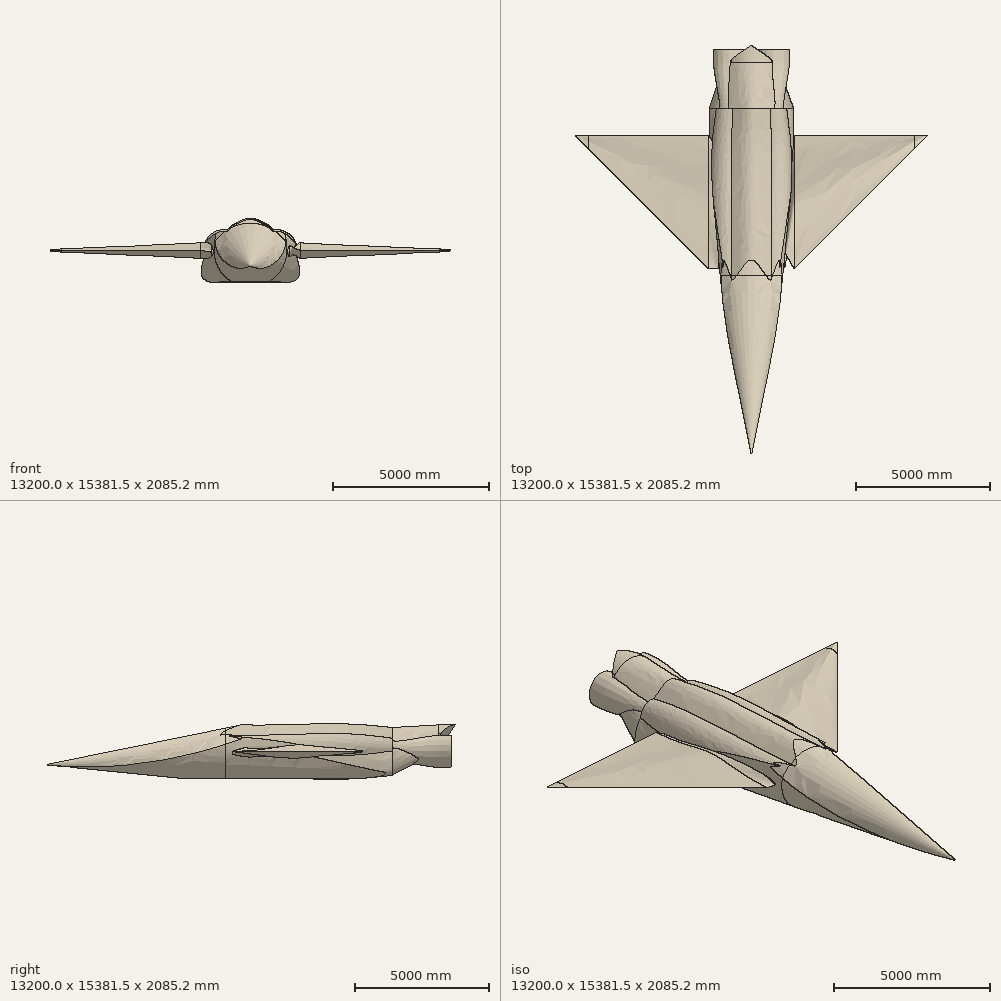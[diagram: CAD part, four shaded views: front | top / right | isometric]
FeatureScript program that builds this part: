
annotation { "Feature Type Name" : "Feature", "Feature Type Description" : "" }
export const myFeature = defineFeature(function(context is Context, id is Id, definition is map)
    precondition{}
    {
        {
            var Q0;
            Q0=qCreatedBy(makeId("Front.planeOp"),FACE);
            cPlane(context, id + "F0", {"entities" : qUnion([Q0]), "cplaneType" : CPlaneType.OFFSET, "offset" : 1750 * mm, "width" : 152.4 * mm, "height" : 152.4 * mm});
        }
        {
            var Q0;
            Q0=qCreatedBy(id+"F0.planeOp",FACE);
            var sketch = newSketch(context, id + "F1", { "sketchPlane" : qUnion([Q0])});
            skLineSegment(sketch, "E0.top", {"start": v(-1394.2, -1000) * mm, "end": v(1394.2, -1000) * mm});
            skPoint(sketch, "E0.middle", {"position": v(0, 0) * mm});
            skFitSpline(sketch, "E1", {"points": [v(-1600, -1000) * mm, v(-848, 530) * mm, v(0, 1000) * mm, v(848, 530) * mm, v(1600, -1000) * mm], "startDerivative": vector(0, 10524.75) * mm, "endDerivative": vector(0, -10524.75) * mm});
            skArc(sketch, "E2", {"start": v(-735.27, 618.52) * mm, "mid": v(-1273.27, 435.52) * mm, "end": v(-1440.68, -107.53) * mm});
            skArc(sketch, "E3.trimOffspring", {"start": v(1440.68, -107.53) * mm, "mid": v(1273.27, 435.52) * mm, "end": v(735.27, 618.52) * mm});
            skFitSpline(sketch, "E4.trimOffspring", {"points": [v(-1600, -1000) * mm, v(-848, 530) * mm, v(0, 1000) * mm, v(848, 530) * mm, v(1600, -1000) * mm], "startDerivative": vector(0, 10524.75) * mm, "endDerivative": vector(0, -10524.75) * mm});
            skFitSpline(sketch, "E5.trimOffspring", {"points": [v(-1600, -1000) * mm, v(-848, 530) * mm, v(0, 1000) * mm, v(848, 530) * mm, v(1600, -1000) * mm], "startDerivative": vector(0, 10524.75) * mm, "endDerivative": vector(0, -10524.75) * mm});
            skArc(sketch, "E6.filletArc", {"start": v(-1593.82, -787.83) * mm, "mid": v(-1539.85, -937.05) * mm, "end": v(-1394.2, -1000) * mm});
            skArc(sketch, "E7.filletArc", {"start": v(1394.2, -1000) * mm, "mid": v(1539.85, -937.05) * mm, "end": v(1593.82, -787.83) * mm});
            skSolve(sketch);
        }
        {
            var Q0;
            Q0=qCreatedBy(makeId("Front.planeOp"),FACE);
            var sketch = newSketch(context, id + "F2", { "sketchPlane" : qUnion([Q0])});
            skLineSegment(sketch, "E8.top", {"start": v(-1394.2, -1000) * mm, "end": v(1394.2, -1000) * mm});
            skPoint(sketch, "E8.middle", {"position": v(0, 0) * mm});
            skFitSpline(sketch, "E9", {"points": [v(-1600, -1000) * mm, v(-848, 530) * mm, v(0, 1000) * mm, v(848, 530) * mm, v(1600, -1000) * mm], "startDerivative": vector(0, 10524.75) * mm, "endDerivative": vector(0, -10524.75) * mm});
            skArc(sketch, "E10", {"start": v(-735.27, 618.52) * mm, "mid": v(-1273.27, 435.52) * mm, "end": v(-1440.68, -107.53) * mm});
            skArc(sketch, "E11.trimOffspring", {"start": v(1440.68, -107.53) * mm, "mid": v(1273.27, 435.52) * mm, "end": v(735.27, 618.52) * mm});
            skFitSpline(sketch, "E12.trimOffspring", {"points": [v(-1600, -1000) * mm, v(-848, 530) * mm, v(0, 1000) * mm, v(848, 530) * mm, v(1600, -1000) * mm], "startDerivative": vector(0, 10524.75) * mm, "endDerivative": vector(0, -10524.75) * mm});
            skFitSpline(sketch, "E13.trimOffspring", {"points": [v(-1600, -1000) * mm, v(-848, 530) * mm, v(0, 1000) * mm, v(848, 530) * mm, v(1600, -1000) * mm], "startDerivative": vector(0, 10524.75) * mm, "endDerivative": vector(0, -10524.75) * mm});
            skArc(sketch, "E14.filletArc", {"start": v(-1593.82, -787.83) * mm, "mid": v(-1539.85, -937.05) * mm, "end": v(-1394.2, -1000) * mm});
            skArc(sketch, "E15.filletArc", {"start": v(1394.2, -1000) * mm, "mid": v(1539.85, -937.05) * mm, "end": v(1593.82, -787.83) * mm});
            skSolve(sketch);
        }
        {
            var Q0;
            Q0=qCreatedBy(makeId("Front.planeOp"),FACE);
            cPlane(context, id + "F3", {"entities" : qUnion([Q0]), "cplaneType" : CPlaneType.OFFSET, "offset" : 3500 * mm, "oppositeDirection" : true, "width" : 150 * mm, "height" : 150 * mm});
        }
        {
            var Q0;
            Q0=qCreatedBy(id+"F3.planeOp",FACE);
            var sketch = newSketch(context, id + "F4", { "sketchPlane" : qUnion([Q0])});
            skLineSegment(sketch, "E16.top", {"start": v(-1394.2, -1000) * mm, "end": v(1394.2, -1000) * mm});
            skPoint(sketch, "E16.middle", {"position": v(0, 0) * mm});
            skFitSpline(sketch, "E17", {"points": [v(-1600, -1000) * mm, v(-848, 530) * mm, v(0, 1000) * mm, v(848, 530) * mm, v(1600, -1000) * mm], "startDerivative": vector(0, 10524.75) * mm, "endDerivative": vector(0, -10524.75) * mm});
            skArc(sketch, "E18", {"start": v(-735.27, 618.52) * mm, "mid": v(-1273.27, 435.52) * mm, "end": v(-1440.68, -107.53) * mm});
            skArc(sketch, "E19.trimOffspring", {"start": v(1440.68, -107.53) * mm, "mid": v(1273.27, 435.52) * mm, "end": v(735.27, 618.52) * mm});
            skFitSpline(sketch, "E20.trimOffspring", {"points": [v(-1600, -1000) * mm, v(-848, 530) * mm, v(0, 1000) * mm, v(848, 530) * mm, v(1600, -1000) * mm], "startDerivative": vector(0, 10524.75) * mm, "endDerivative": vector(0, -10524.75) * mm});
            skFitSpline(sketch, "E21.trimOffspring", {"points": [v(-1600, -1000) * mm, v(-848, 530) * mm, v(0, 1000) * mm, v(848, 530) * mm, v(1600, -1000) * mm], "startDerivative": vector(0, 10524.75) * mm, "endDerivative": vector(0, -10524.75) * mm});
            skArc(sketch, "E22.filletArc", {"start": v(-1593.82, -787.83) * mm, "mid": v(-1539.85, -937.05) * mm, "end": v(-1394.2, -1000) * mm});
            skArc(sketch, "E23.filletArc", {"start": v(1394.2, -1000) * mm, "mid": v(1539.85, -937.05) * mm, "end": v(1593.82, -787.83) * mm});
            skSolve(sketch);
        }
        {
            var Q0;
            Q0=qCreatedBy(makeId("Front.planeOp"),FACE);
            cPlane(context, id + "F5", {"entities" : qUnion([Q0]), "cplaneType" : CPlaneType.OFFSET, "offset" : 4500 * mm, "oppositeDirection" : true, "width" : 150 * mm, "height" : 150 * mm});
        }
        {
            var Q0;
            Q0=qCreatedBy(id+"F5.planeOp",FACE);
            var sketch = newSketch(context, id + "F6", { "sketchPlane" : qUnion([Q0])});
            skLineSegment(sketch, "E24.top", {"start": v(-1413.07, -900) * mm, "end": v(1413.07, -900) * mm});
            skPoint(sketch, "E24.middle", {"position": v(0, 0) * mm});
            skFitSpline(sketch, "E25", {"points": [v(-1600, -900) * mm, v(-784.42, 441.24) * mm, v(0, 900) * mm, v(784.42, 441.24) * mm, v(1600, -900) * mm], "startDerivative": vector(0, 9508.62) * mm, "endDerivative": vector(0, -9508.62) * mm});
            skArc(sketch, "E26", {"start": v(-719.25, 488.69) * mm, "mid": v(-1131.76, 394.84) * mm, "end": v(-1324.66, 18.33) * mm});
            skArc(sketch, "E27.trimOffspring", {"start": v(1324.66, 18.33) * mm, "mid": v(1131.76, 394.84) * mm, "end": v(719.25, 488.69) * mm});
            skFitSpline(sketch, "E28.trimOffspring", {"points": [v(-1600, -900) * mm, v(-784.42, 441.24) * mm, v(0, 900) * mm, v(784.42, 441.24) * mm, v(1600, -900) * mm], "startDerivative": vector(0, 9508.62) * mm, "endDerivative": vector(0, -9508.62) * mm});
            skFitSpline(sketch, "E29.trimOffspring", {"points": [v(-1600, -900) * mm, v(-784.42, 441.24) * mm, v(0, 900) * mm, v(784.42, 441.24) * mm, v(1600, -900) * mm], "startDerivative": vector(0, 9508.62) * mm, "endDerivative": vector(0, -9508.62) * mm});
            skArc(sketch, "E30.filletArc", {"start": v(-1592.48, -705.43) * mm, "mid": v(-1545.4, -842.02) * mm, "end": v(-1413.07, -900) * mm});
            skArc(sketch, "E31.filletArc", {"start": v(1413.07, -900) * mm, "mid": v(1545.4, -842.02) * mm, "end": v(1592.48, -705.43) * mm});
            skLineSegment(sketch, "E32", {"start": v(-719.25, 488.69) * mm, "end": v(-1324.66, 18.33) * mm, "construction": true});
            skLineSegment(sketch, "E33", {"start": v(719.25, 488.69) * mm, "end": v(1324.66, 18.33) * mm, "construction": true});
            skSolve(sketch);
        }
        {
            var Q0;
            Q0=qCreatedBy(makeId("Front.planeOp"),FACE);
            cPlane(context, id + "F7", {"entities" : qUnion([Q0]), "cplaneType" : CPlaneType.OFFSET, "offset" : 6232.05 * mm, "oppositeDirection" : true, "width" : 150 * mm, "height" : 150 * mm});
        }
        {
            var Q0;
            Q0=qCreatedBy(id+"F7.planeOp",FACE);
            var sketch = newSketch(context, id + "F8", { "sketchPlane" : qUnion([Q0])});
            skArc(sketch, "E34", {"start": v(998.61, 52.63) * mm, "mid": v(0, 1000) * mm, "end": v(-998.61, 52.63) * mm});
            skLineSegment(sketch, "E35", {"start": v(0, 0) * mm, "end": v(-948.68, 0) * mm});
            skLineSegment(sketch, "E36", {"start": v(0, 0) * mm, "end": v(948.68, 0) * mm});
            skPoint(sketch, "E37.visualSharp", {"position": v(-1000, 0) * mm});
            skArc(sketch, "E37.filletArc", {"start": v(-998.61, 52.63) * mm, "mid": v(-984.96, 15.59) * mm, "end": v(-948.68, 0) * mm});
            skPoint(sketch, "E38.visualSharp", {"position": v(1000, 0) * mm});
            skArc(sketch, "E38.filletArc", {"start": v(948.68, 0) * mm, "mid": v(984.96, 15.59) * mm, "end": v(998.61, 52.63) * mm});
            skLineSegment(sketch, "E39", {"start": v(0, 1000) * mm, "end": v(0, 675) * mm, "construction": true});
            skPoint(sketch, "E39.endSnap0", {"position": v(0, 1000) * mm});
            skLineSegment(sketch, "E40", {"start": v(0, 675) * mm, "end": v(737.82, 675) * mm, "construction": true});
            skLineSegment(sketch, "E41", {"start": v(0, 675) * mm, "end": v(-737.82, 675) * mm, "construction": true});
            skSolve(sketch);
        }
        {
            var Q0;
            Q0=qSketchRegion(id+"F1",true);
            var Q1;
            Q1=qSketchRegion(id+"F2",true);
            var Q2;
            Q2=qSketchRegion(id+"F4",true);
            var Q3;
            Q3=qSketchRegion(id+"F6",true);
            loft(context, id + "F9", {"sheetProfilesArray" : [{ "sheetProfileEntities" : qUnion([Q0]) }, { "sheetProfileEntities" : qUnion([Q1]) }, { "sheetProfileEntities" : qUnion([Q2]) }, { "sheetProfileEntities" : qUnion([Q3]) }]});
        }
        {
            var Q0;
            Q0=sQuery(id+"F6.wireOp",EDGE,"E32");
            var Q1;
            Q1=sQuery(id+"F8.wireOp",VERTEX,"E41.end");
            cPlane(context, id + "F10", {"entities" : qUnion([Q0, Q1]), "cplaneType" : CPlaneType.LINE_ANGLE, "offset" : 25 * mm, "angle" : 0 * degree, "width" : 150 * mm, "height" : 150 * mm});
        }
        {
            var Q0;
            Q0=qCreatedBy(id+"F10.planeOp",FACE);
            var sketch = newSketch(context, id + "F11", { "sketchPlane" : qUnion([Q0])});
            skLineSegment(sketch, "E42", {"start": v(-589.34, -4526.34) * mm, "end": v(-612.8, -6268.32) * mm});
            skLineSegment(sketch, "E43", {"start": v(-1354.08, -4472.19) * mm, "end": v(-612.8, -6268.32) * mm});
            skSolve(sketch);
        }
        {
            var Q0;
            Q0=sQuery(id+"F6.wireOp",EDGE,"E33");
            var Q1;
            Q1=sQuery(id+"F8.wireOp",VERTEX,"E40.end");
            cPlane(context, id + "F12", {"entities" : qUnion([Q0, Q1]), "cplaneType" : CPlaneType.LINE_ANGLE, "offset" : 25 * mm, "angle" : 0 * degree, "width" : 150 * mm, "height" : 150 * mm});
        }
        {
            var Q0;
            Q0=qCreatedBy(id+"F12.planeOp",FACE);
            var sketch = newSketch(context, id + "F13", { "sketchPlane" : qUnion([Q0])});
            skLineSegment(sketch, "E44", {"start": v(589.34, 4526.34) * mm, "end": v(612.8, 6268.32) * mm});
            skLineSegment(sketch, "E45", {"start": v(1354.08, 4472.19) * mm, "end": v(612.8, 6268.32) * mm});
            skSolve(sketch);
        }
        {
            var Q1;
            Q1=makeQuery(id+"F6.imprint","IMPRINT",FACE,{"disambiguationData":[TD([[makeQuery(id+"F6.imprint","IMPRINT",EDGE,{"derivedFrom":sQuery(id+"F6.wireOp",EDGE,"E24.top")}),1.0]])]});
            var Q2;
            Q2=makeQuery(id+"F8.imprint","IMPRINT",FACE,{"disambiguationData":[TD([[makeQuery(id+"F8.imprint","IMPRINT",EDGE,{"derivedFrom":sQuery(id+"F8.wireOp",EDGE,"E34")}),1.0]])]});
            var Q3;
            Q3=sQuery(id+"F11.wireOp",EDGE,"E42");
            var Q4;
            Q4=sQuery(id+"F13.wireOp",EDGE,"E44");
            loft(context, id + "F14", {"operationType" : NewBodyOperationType.ADD, "addGuides" : true, "sheetProfilesArray" : [{ "sheetProfileEntities" : qUnion([Q1]) }, { "sheetProfileEntities" : qUnion([Q2]) }], "guidesArray" : [{ "guideEntities" : qUnion([Q3]), "guideDerivativeType" : LoftGuideDerivativeType.DEFAULT, "guideDerivativeMagnitude" : 1 }, { "guideEntities" : qUnion([Q4]), "guideDerivativeType" : LoftGuideDerivativeType.DEFAULT, "guideDerivativeMagnitude" : 1 }]});
        }
        {
            var Q0;
            Q0=makeQuery(id+"F14.opLoft","CAP_FACE",FACE,{"disambiguationData":[OSD([makeQuery(id+"F8.imprint","IMPRINT",FACE,{"disambiguationData":[TD([[makeQuery(id+"F8.imprint","IMPRINT",EDGE,{"derivedFrom":sQuery(id+"F8.wireOp",EDGE,"E34")}),1.0]])]})])],"isStart":true});
            extrude(context, id + "F15", {"entities" : qUnion([Q0]), "operationType" : NewBodyOperationType.ADD, "depth" : 649.4 * mm});
        }
        {
            var Q0;
            Q0=qCreatedBy(makeId("Right.planeOp"),FACE);
            var sketch = newSketch(context, id + "F16", { "sketchPlane" : qUnion([Q0])});
            skLineSegment(sketch, "E46", {"start": v(0, 0) * mm, "end": v(4500, 0) * mm});
            skLineSegment(sketch, "E47", {"start": v(4500, 0) * mm, "end": v(6232.05, 0) * mm});
            skLineSegment(sketch, "E48", {"start": v(4500, 0) * mm, "end": v(4500, 1000) * mm});
            skLineSegment(sketch, "E49", {"start": v(4500, 1000) * mm, "end": v(6881.46, 1000) * mm});
            skLineSegment(sketch, "E50", {"start": v(6881.46, 1000) * mm, "end": v(6881.46, -1000) * mm});
            skLineSegment(sketch, "E51", {"start": v(6881.46, 1000) * mm, "end": v(6232.05, 0) * mm});
            skLineSegment(sketch, "E52", {"start": v(6232.05, 0) * mm, "end": v(5582.64, -1000) * mm});
            skLineSegment(sketch, "E53", {"start": v(5582.64, -1000) * mm, "end": v(6881.46, -1000) * mm});
            skSolve(sketch);
        }
        {
            var Q0;
            Q0=makeQuery(id+"F16.imprint","IMPRINT",FACE,{"disambiguationData":[TD([[makeQuery(id+"F16.imprint","IMPRINT",EDGE,{"derivedFrom":sQuery(id+"F16.wireOp",EDGE,"E50")}),-1.0]])]});
            var Q1;
            Q1=sQuery(id+"F16.wireOp",EDGE,"E49");
            revolve(context, id + "F17", {"operationType" : NewBodyOperationType.REMOVE, "entities" : qUnion([Q0]), "axis" : qUnion([Q1]), "revolveType" : RevolveType.SYMMETRIC, "oppositeDirection" : true, "angle" : 182 * degree});
        }
        {
            var Q0;
            Q0=makeQuery(id+"F9.opLoft","CAP_FACE",FACE,{"disambiguationData":[OSD([makeQuery(id+"F1.imprint","IMPRINT",FACE,{"disambiguationData":[TD([[makeQuery(id+"F1.imprint","IMPRINT",EDGE,{"derivedFrom":sQuery(id+"F1.wireOp",EDGE,"E0.top")}),1.0]])]})])],"isStart":true});
            extrude(context, id + "F18", {"entities" : qUnion([Q0]), "depth" : 6750 * mm});
        }
        {
            var Q0;
            Q0=qCreatedBy(makeId("Right.planeOp"),FACE);
            var sketch = newSketch(context, id + "F19", { "sketchPlane" : qUnion([Q0])});
            skLineSegment(sketch, "E54", {"start": v(0, 0) * mm, "end": v(-3500, 0) * mm});
            skLineSegment(sketch, "E55", {"start": v(-3500, 0) * mm, "end": v(-3500, -1000) * mm});
            skLineSegment(sketch, "E56", {"start": v(-3500, -1000) * mm, "end": v(-8500, -1000) * mm});
            skLineSegment(sketch, "E57", {"start": v(-8500, -1000) * mm, "end": v(-8500, -499.31) * mm});
            skLineSegment(sketch, "E58", {"start": v(-1151.4, 0) * mm, "end": v(-1151.4, 1000) * mm});
            skLineSegment(sketch, "E59", {"start": v(-1151.4, 1000) * mm, "end": v(-8500, -499.31) * mm});
            skLineSegment(sketch, "E60", {"start": v(-8500, -499.31) * mm, "end": v(-3500, -1000) * mm});
            skLineSegment(sketch, "E61", {"start": v(-1151.4, 1000) * mm, "end": v(-8500, 1000) * mm});
            skLineSegment(sketch, "E62", {"start": v(-8500, 1000) * mm, "end": v(-8500, -499.31) * mm});
            skLineSegment(sketch, "E63", {"start": v(-8500, -1000) * mm, "end": v(-8500, -1980) * mm});
            skLineSegment(sketch, "E64", {"start": v(-3500, -1000) * mm, "end": v(6286.5, -1980) * mm});
            skLineSegment(sketch, "E65", {"start": v(6286.5, -1980) * mm, "end": v(-8500, -1980) * mm});
            skLineSegment(sketch, "E66", {"start": v(-8500, -499.31) * mm, "end": v(-3500, -499.31) * mm});
            skSolve(sketch);
        }
        {
            var Q0;
            Q0=makeQuery(id+"F19.imprint","IMPRINT",FACE,{"disambiguationData":[TD([[makeQuery(id+"F19.imprint","IMPRINT",EDGE,{"derivedFrom":sQuery(id+"F19.wireOp",EDGE,"E59")}),-1.0]])]});
            var Q1;
            Q1=sQuery(id+"F19.wireOp",EDGE,"E66");
            revolve(context, id + "F20", {"operationType" : NewBodyOperationType.REMOVE, "entities" : qUnion([Q0]), "axis" : qUnion([Q1]), "revolveType" : RevolveType.SYMMETRIC, "oppositeDirection" : true, "angle" : 250 * degree});
        }
        {
            var Q0;
            Q0=makeQuery(id+"F19.imprint","IMPRINT",FACE,{"disambiguationData":[TD([[makeQuery(id+"F19.imprint","IMPRINT",EDGE,{"derivedFrom":sQuery(id+"F19.wireOp",EDGE,"E56")}),-1.0]])]});
            var Q1;
            Q1=makeQuery(id+"F19.imprint","IMPRINT",FACE,{"disambiguationData":[TD([[makeQuery(id+"F19.imprint","IMPRINT",EDGE,{"derivedFrom":sQuery(id+"F19.wireOp",EDGE,"E56")}),1.0]])]});
            var Q2;
            Q2=sQuery(id+"F19.wireOp",EDGE,"E54");
            revolve(context, id + "F21", {"operationType" : NewBodyOperationType.REMOVE, "entities" : qUnion([Q0, Q1]), "axis" : qUnion([Q2]), "revolveType" : RevolveType.SYMMETRIC, "oppositeDirection" : true, "angle" : 240 * degree});
        }
        {
            var Q0;
            Q0=qCreatedBy(makeId("Front.planeOp"),FACE);
            cPlane(context, id + "F22", {"entities" : qUnion([Q0]), "cplaneType" : CPlaneType.OFFSET, "offset" : 3500 * mm, "oppositeDirection" : true, "width" : 150 * mm, "height" : 150 * mm});
        }
        {
            var Q0;
            Q0=qCreatedBy(id+"F22.planeOp",FACE);
            var sketch = newSketch(context, id + "F23", { "sketchPlane" : qUnion([Q0])});
            skCircle(sketch, "E67", {"center": v(-825, 0) * mm, "radius": 600 * mm});
            skCircle(sketch, "E68", {"center": v(825, 0) * mm, "radius": 600 * mm});
            skSolve(sketch);
        }
        {
            var Q0;
            Q0=qCreatedBy(makeId("Front.planeOp"),FACE);
            cPlane(context, id + "F24", {"entities" : qUnion([Q0]), "cplaneType" : CPlaneType.OFFSET, "offset" : 4500 * mm, "oppositeDirection" : true, "width" : 150 * mm, "height" : 150 * mm});
        }
        {
            var Q0;
            Q0=qCreatedBy(id+"F24.planeOp",FACE);
            var sketch = newSketch(context, id + "F25", { "sketchPlane" : qUnion([Q0])});
            skCircle(sketch, "E69", {"center": v(-825, 0) * mm, "radius": 400 * mm});
            skCircle(sketch, "E70", {"center": v(825, 0) * mm, "radius": 400 * mm});
            skSolve(sketch);
        }
        {
            var Q0;
            Q0=qCreatedBy(makeId("Front.planeOp"),FACE);
            cPlane(context, id + "F26", {"entities" : qUnion([Q0]), "cplaneType" : CPlaneType.OFFSET, "offset" : 6232.05 * mm, "oppositeDirection" : true, "width" : 150 * mm, "height" : 150 * mm});
        }
        {
            var Q0;
            Q0=qCreatedBy(id+"F26.planeOp",FACE);
            var sketch = newSketch(context, id + "F27", { "sketchPlane" : qUnion([Q0])});
            skCircle(sketch, "E71", {"center": v(-825, 0) * mm, "radius": 600 * mm});
            skCircle(sketch, "E72", {"center": v(825, 0) * mm, "radius": 600 * mm});
            skSolve(sketch);
        }
        {
            var Q0;
            Q0=qCreatedBy(makeId("Front.planeOp"),FACE);
            cPlane(context, id + "F28", {"entities" : qUnion([Q0]), "cplaneType" : CPlaneType.OFFSET, "offset" : 6732.05 * mm, "oppositeDirection" : true, "width" : 150 * mm, "height" : 150 * mm});
        }
        {
            var Q0;
            Q0=qCreatedBy(id+"F28.planeOp",FACE);
            var sketch = newSketch(context, id + "F29", { "sketchPlane" : qUnion([Q0])});
            skCircle(sketch, "E73", {"center": v(-825, 0) * mm, "radius": 600 * mm});
            skCircle(sketch, "E74", {"center": v(825, 0) * mm, "radius": 600 * mm});
            skSolve(sketch);
        }
        {
            var Q0;
            Q0=makeQuery(id+"F23.imprint","IMPRINT",FACE,{"disambiguationData":[TD([[makeQuery(id+"F23.imprint","IMPRINT",EDGE,{"derivedFrom":sQuery(id+"F23.wireOp",EDGE,"E67")}),1.0]])]});
            var Q1;
            Q1=makeQuery(id+"F25.imprint","IMPRINT",FACE,{"disambiguationData":[TD([[makeQuery(id+"F25.imprint","IMPRINT",EDGE,{"derivedFrom":sQuery(id+"F25.wireOp",EDGE,"E69")}),1.0]])]});
            var Q2;
            Q2=makeQuery(id+"F27.imprint","IMPRINT",FACE,{"disambiguationData":[TD([[makeQuery(id+"F27.imprint","IMPRINT",EDGE,{"derivedFrom":sQuery(id+"F27.wireOp",EDGE,"E71")}),1.0]])]});
            var Q3;
            Q3=makeQuery(id+"F29.imprint","IMPRINT",FACE,{"disambiguationData":[TD([[makeQuery(id+"F29.imprint","IMPRINT",EDGE,{"derivedFrom":sQuery(id+"F29.wireOp",EDGE,"E73")}),1.0]])]});
            loft(context, id + "F30", {"sheetProfilesArray" : [{ "sheetProfileEntities" : qUnion([Q0]) }, { "sheetProfileEntities" : qUnion([Q1]) }, { "sheetProfileEntities" : qUnion([Q2]) }, { "sheetProfileEntities" : qUnion([Q3]) }]});
        }
        {
            var Q0;
            Q0=makeQuery(id+"F23.imprint","IMPRINT",FACE,{"disambiguationData":[TD([[makeQuery(id+"F23.imprint","IMPRINT",EDGE,{"derivedFrom":sQuery(id+"F23.wireOp",EDGE,"E68")}),1.0]])]});
            var Q1;
            Q1=makeQuery(id+"F25.imprint","IMPRINT",FACE,{"disambiguationData":[TD([[makeQuery(id+"F25.imprint","IMPRINT",EDGE,{"derivedFrom":sQuery(id+"F25.wireOp",EDGE,"E70")}),1.0]])]});
            var Q2;
            Q2=makeQuery(id+"F27.imprint","IMPRINT",FACE,{"disambiguationData":[TD([[makeQuery(id+"F27.imprint","IMPRINT",EDGE,{"derivedFrom":sQuery(id+"F27.wireOp",EDGE,"E72")}),1.0]])]});
            var Q3;
            Q3=makeQuery(id+"F29.imprint","IMPRINT",FACE,{"disambiguationData":[TD([[makeQuery(id+"F29.imprint","IMPRINT",EDGE,{"derivedFrom":sQuery(id+"F29.wireOp",EDGE,"E74")}),1.0]])]});
            loft(context, id + "F31", {"sheetProfilesArray" : [{ "sheetProfileEntities" : qUnion([Q0]) }, { "sheetProfileEntities" : qUnion([Q1]) }, { "sheetProfileEntities" : qUnion([Q2]) }, { "sheetProfileEntities" : qUnion([Q3]) }]});
        }
        {
            var Q0;
            Q0=qCreatedBy(makeId("Top.planeOp"),FACE);
            var sketch = newSketch(context, id + "F32", { "sketchPlane" : qUnion([Q0])});
            skLineSegment(sketch, "E75", {"start": v(0, 0) * mm, "end": v(0, 1000) * mm});
            skLineSegment(sketch, "E76", {"start": v(0, 1000) * mm, "end": v(-1600, 1000) * mm});
            skLineSegment(sketch, "E77", {"start": v(-1600, 1000) * mm, "end": v(-1600, -1500) * mm});
            skLineSegment(sketch, "E78", {"start": v(-1600, 1000) * mm, "end": v(-1600, 3500) * mm});
            skLineSegment(sketch, "E79", {"start": v(-1600, 3500) * mm, "end": v(-6100, 3500) * mm});
            skLineSegment(sketch, "E80", {"start": v(-6100, 3500) * mm, "end": v(-6600, 3500) * mm});
            skLineSegment(sketch, "E81", {"start": v(-6100, 3500) * mm, "end": v(-6100, 3000) * mm});
            skLineSegment(sketch, "E82", {"start": v(-1600, -1500) * mm, "end": v(-6100, 3000) * mm});
            skLineSegment(sketch, "E83", {"start": v(0, 1000) * mm, "end": v(1600, 1000) * mm});
            skLineSegment(sketch, "E84", {"start": v(1600, 1000) * mm, "end": v(1600, -1500) * mm});
            skLineSegment(sketch, "E85", {"start": v(1600, 1000) * mm, "end": v(1600, 3500) * mm});
            skLineSegment(sketch, "E86", {"start": v(1600, 3500) * mm, "end": v(6100, 3500) * mm});
            skLineSegment(sketch, "E87", {"start": v(6100, 3500) * mm, "end": v(6600, 3500) * mm});
            skLineSegment(sketch, "E88", {"start": v(6100, 3500) * mm, "end": v(6100, 3000) * mm});
            skLineSegment(sketch, "E89", {"start": v(1600, -1500) * mm, "end": v(6100, 3000) * mm});
            skSolve(sketch);
        }
        {
            var Q0;
            Q0=qCreatedBy(makeId("Right.planeOp"),FACE);
            var sketch = newSketch(context, id + "F33", { "sketchPlane" : qUnion([Q0])});
            skFitSpline(sketch, "E90", {"points": [v(-1500, -50) * mm, v(0, 250) * mm, v(3000, -50) * mm, v(0, -250) * mm, v(-1500, -50) * mm]});
            skSolve(sketch);
        }
        {
            var Q0;
            Q0=qCreatedBy(makeId("Right.planeOp"),FACE);
            cPlane(context, id + "F34", {"entities" : qUnion([Q0]), "cplaneType" : CPlaneType.OFFSET, "offset" : 1600 * mm, "oppositeDirection" : true, "width" : 150 * mm, "height" : 150 * mm});
        }
        {
            var Q0;
            Q0=qCreatedBy(id+"F34.planeOp",FACE);
            var sketch = newSketch(context, id + "F35", { "sketchPlane" : qUnion([Q0])});
            skFitSpline(sketch, "E91", {"points": [v(-1500, 0) * mm, v(1000, 250) * mm, v(3500, 0) * mm], "startDerivative": vector(7500, 0) * mm, "endDerivative": vector(7500, 0) * mm});
            skFitSpline(sketch, "E92", {"points": [v(-1500, 0) * mm, v(1000, -250) * mm, v(3500, 0) * mm], "startDerivative": vector(5000, -750) * mm, "endDerivative": vector(7500, 0) * mm});
            skSolve(sketch);
        }
        {
            var Q0;
            Q0=qCreatedBy(makeId("Right.planeOp"),FACE);
            cPlane(context, id + "F36", {"entities" : qUnion([Q0]), "cplaneType" : CPlaneType.OFFSET, "offset" : 1600 * mm, "width" : 150 * mm, "height" : 150 * mm});
        }
        {
            var Q0;
            Q0=qCreatedBy(id+"F36.planeOp",FACE);
            var sketch = newSketch(context, id + "F37", { "sketchPlane" : qUnion([Q0])});
            skFitSpline(sketch, "E93", {"points": [v(-1500, 0) * mm, v(1000, 250) * mm, v(3500, 0) * mm], "startDerivative": vector(7500, 0) * mm, "endDerivative": vector(7500, 0) * mm});
            skFitSpline(sketch, "E94", {"points": [v(-1500, 0) * mm, v(1000, -250) * mm, v(3500, 0) * mm], "startDerivative": vector(5000, -750) * mm, "endDerivative": vector(7500, 0) * mm});
            skSolve(sketch);
        }
        {
            var Q0;
            Q0=qCreatedBy(makeId("Right.planeOp"),FACE);
            cPlane(context, id + "F38", {"entities" : qUnion([Q0]), "cplaneType" : CPlaneType.OFFSET, "offset" : 6100 * mm, "oppositeDirection" : true, "width" : 150 * mm, "height" : 150 * mm});
        }
        {
            var Q0;
            Q0=qCreatedBy(id+"F38.planeOp",FACE);
            var sketch = newSketch(context, id + "F39", { "sketchPlane" : qUnion([Q0])});
            skFitSpline(sketch, "E95", {"points": [v(3000, 0) * mm, v(3250, 50) * mm, v(3500, 0) * mm], "startDerivative": vector(750, 0) * mm, "endDerivative": vector(750, 0) * mm});
            skFitSpline(sketch, "E96", {"points": [v(3000, 0) * mm, v(3250, -50) * mm, v(3500, 0) * mm], "startDerivative": vector(500, -150) * mm, "endDerivative": vector(750, 0) * mm});
            skSolve(sketch);
        }
        {
            var Q0;
            Q0=qCreatedBy(makeId("Right.planeOp"),FACE);
            cPlane(context, id + "F40", {"entities" : qUnion([Q0]), "cplaneType" : CPlaneType.OFFSET, "offset" : 6100 * mm, "width" : 150 * mm, "height" : 150 * mm});
        }
        {
            var Q0;
            Q0=qCreatedBy(id+"F40.planeOp",FACE);
            var sketch = newSketch(context, id + "F41", { "sketchPlane" : qUnion([Q0])});
            skFitSpline(sketch, "E97", {"points": [v(3000, 0) * mm, v(3250, 50) * mm, v(3500, 0) * mm], "startDerivative": vector(850.99, 0) * mm, "endDerivative": vector(750, 0) * mm});
            skFitSpline(sketch, "E98", {"points": [v(3000, 0) * mm, v(3250, -50) * mm, v(3500, 0) * mm], "startDerivative": vector(500, -150) * mm, "endDerivative": vector(750, 0) * mm});
            skSolve(sketch);
        }
        {
            var Q0;
            Q0=qSketchRegion(id+"F33",true);
            extrude(context, id + "F42", {"entities" : qUnion([Q0]), "endBound" : BoundingType.SYMMETRIC, "depth" : 2500 * mm});
        }
        {
            var Q1;
            Q1=makeQuery(id+"F42.opExtrude","CAP_FACE",FACE,{"disambiguationData":[OSD([sQuery(id+"F33.wireOp",EDGE,"E90")])],"isStart":true});
            var Q2;
            {var subQ0=sQuery(id+"F35.wireOp",EDGE,"E91");Q2=makeQuery(id+"F35.imprint","IMPRINT",FACE,{"disambiguationData":[TD([[makeQuery(id+"F35.imprint","IMPRINT",EDGE,{"derivedFrom":subQ0}),-1.0]])]});}
            loft(context, id + "F43", {"operationType" : NewBodyOperationType.ADD, "sheetProfilesArray" : [{ "sheetProfileEntities" : qUnion([Q1]) }, { "sheetProfileEntities" : qUnion([Q2]) }]});
        }
        {
            var Q1;
            Q1=makeQuery(id+"F42.opExtrude","CAP_FACE",FACE,{"disambiguationData":[OSD([sQuery(id+"F33.wireOp",EDGE,"E90")])],"isStart":false});
            var Q2;
            {var subQ0=sQuery(id+"F37.wireOp",EDGE,"E93");Q2=makeQuery(id+"F37.imprint","IMPRINT",FACE,{"disambiguationData":[TD([[makeQuery(id+"F37.imprint","IMPRINT",EDGE,{"derivedFrom":subQ0}),-1.0]])]});}
            loft(context, id + "F44", {"operationType" : NewBodyOperationType.ADD, "sheetProfilesArray" : [{ "sheetProfileEntities" : qUnion([Q1]) }, { "sheetProfileEntities" : qUnion([Q2]) }]});
        }
        {
            var Q1;
            {var subQ0=sQuery(id+"F35.wireOp",EDGE,"E91");Q1=makeQuery(id+"F43.opLoft","CAP_FACE",FACE,{"disambiguationData":[OSD([makeQuery(id+"F35.imprint","IMPRINT",FACE,{"disambiguationData":[TD([[makeQuery(id+"F35.imprint","IMPRINT",EDGE,{"derivedFrom":subQ0}),-1.0]])]})])],"isStart":true});}
            var Q2;
            {var subQ0=sQuery(id+"F39.wireOp",EDGE,"E95");Q2=makeQuery(id+"F39.imprint","IMPRINT",FACE,{"disambiguationData":[TD([[makeQuery(id+"F39.imprint","IMPRINT",EDGE,{"derivedFrom":subQ0}),-1.0]])]});}
            loft(context, id + "F45", {"operationType" : NewBodyOperationType.ADD, "sheetProfilesArray" : [{ "sheetProfileEntities" : qUnion([Q1]) }, { "sheetProfileEntities" : qUnion([Q2]) }]});
        }
        {
            var Q1;
            {var subQ0=sQuery(id+"F37.wireOp",EDGE,"E93");Q1=makeQuery(id+"F44.opLoft","CAP_FACE",FACE,{"disambiguationData":[OSD([makeQuery(id+"F37.imprint","IMPRINT",FACE,{"disambiguationData":[TD([[makeQuery(id+"F37.imprint","IMPRINT",EDGE,{"derivedFrom":subQ0}),-1.0]])]})])],"isStart":true});}
            var Q2;
            {var subQ0=sQuery(id+"F41.wireOp",EDGE,"E97");Q2=makeQuery(id+"F41.imprint","IMPRINT",FACE,{"disambiguationData":[TD([[makeQuery(id+"F41.imprint","IMPRINT",EDGE,{"derivedFrom":subQ0}),-1.0]])]});}
            loft(context, id + "F46", {"operationType" : NewBodyOperationType.ADD, "sheetProfilesArray" : [{ "sheetProfileEntities" : qUnion([Q1]) }, { "sheetProfileEntities" : qUnion([Q2]) }]});
        }
        {
            var Q1;
            {var subQ0=sQuery(id+"F39.wireOp",EDGE,"E95");Q1=makeQuery(id+"F45.opLoft","CAP_FACE",FACE,{"disambiguationData":[OSD([makeQuery(id+"F39.imprint","IMPRINT",FACE,{"disambiguationData":[TD([[makeQuery(id+"F39.imprint","IMPRINT",EDGE,{"derivedFrom":subQ0}),-1.0]])]})])],"isStart":true});}
            var Q2;
            Q2=sQuery(id+"F32.wireOp",VERTEX,"E80.end");
            loft(context, id + "F47", {"operationType" : NewBodyOperationType.ADD, "sheetProfilesArray" : [{ "sheetProfileEntities" : qUnion([Q1]) }, { "sheetProfileEntities" : qUnion([Q2]) }]});
        }
        {
            var Q1;
            {var subQ0=sQuery(id+"F41.wireOp",EDGE,"E97");Q1=makeQuery(id+"F46.opLoft","CAP_FACE",FACE,{"disambiguationData":[OSD([makeQuery(id+"F41.imprint","IMPRINT",FACE,{"disambiguationData":[TD([[makeQuery(id+"F41.imprint","IMPRINT",EDGE,{"derivedFrom":subQ0}),-1.0]])]})])],"isStart":true});}
            var Q2;
            Q2=sQuery(id+"F32.wireOp",VERTEX,"E87.end");
            loft(context, id + "F48", {"operationType" : NewBodyOperationType.ADD, "sheetProfilesArray" : [{ "sheetProfileEntities" : qUnion([Q1]) }, { "sheetProfileEntities" : qUnion([Q2]) }]});
        }
    });
